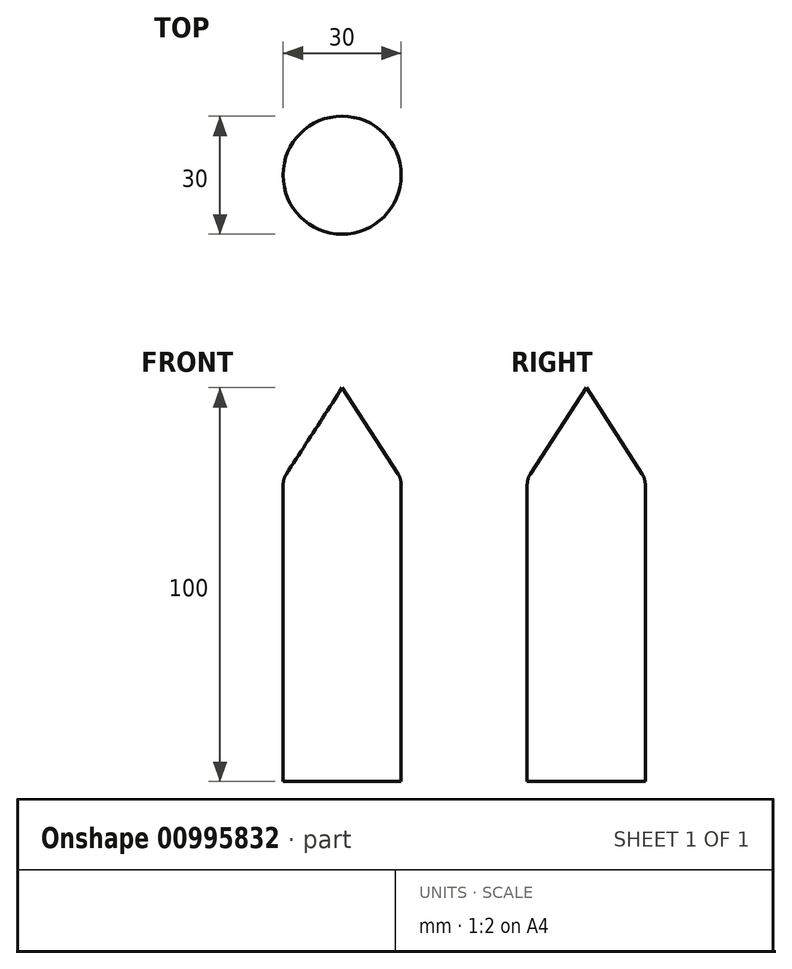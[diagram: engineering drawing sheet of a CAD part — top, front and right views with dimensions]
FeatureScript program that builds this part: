
annotation { "Feature Type Name" : "Feature", "Feature Type Description" : "" }
export const myFeature = defineFeature(function(context is Context, id is Id, definition is map)
    precondition{}
    {
        {
            var Q0;
            Q0=qCreatedBy(makeId("Front.planeOp"),FACE);
            var sketch = newSketch(context, id + "F0", { "sketchPlane" : qUnion([Q0])});
            skLineSegment(sketch, "E0", {"start": v(0, 0) * mm, "end": v(0, 337.3) * mm, "construction": true});
            skLineSegment(sketch, "E1", {"start": v(0, 100) * mm, "end": v(15, 76.84) * mm});
            skLineSegment(sketch, "E2", {"start": v(15, 76.84) * mm, "end": v(15, 0) * mm});
            skLineSegment(sketch, "E3", {"start": v(15, 0) * mm, "end": v(0, 0) * mm});
            skLineSegment(sketch, "E4", {"start": v(0, 100) * mm, "end": v(0, 0) * mm});
            skSolve(sketch);
        }
        {
            var Q0;
            Q0=makeQuery(id+"F0.imprint","IMPRINT",FACE,{"disambiguationData":[TD([[makeQuery(id+"F0.imprint","IMPRINT",EDGE,{"derivedFrom":sQuery(id+"F0.wireOp",EDGE,"E1")}),-1.0]])]});
            var Q1;
            Q1=sQuery(id+"F0.wireOp",EDGE,"E0");
            revolve(context, id + "F1", {"surfaceOperationType" : NewSurfaceOperationType.NEW, "entities" : qUnion([Q0]), "axis" : qUnion([Q1]), "revolveType" : RevolveType.FULL});
        }
        {
            var Q0;
            Q0=makeQuery(id+"F1.opRevolve","SWEPT_EDGE",EDGE,{"disambiguationData":[OSD([sQuery(id+"F0.wireOp",EDGE,"E1"),sQuery(id+"F0.wireOp",EDGE,"E2")])]});
            fillet(context, id + "F2", {"entities" : qUnion([Q0]), "radius" : 5 * mm, "tangentPropagation" : true, "allowEdgeOverflow" : false});
        }
    });
